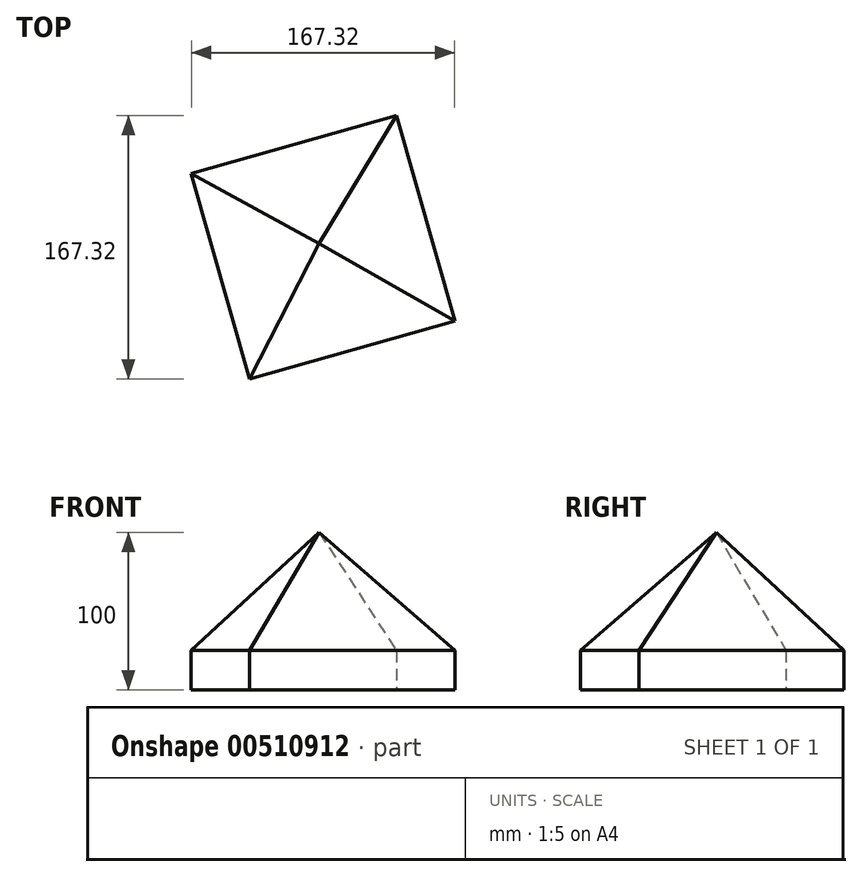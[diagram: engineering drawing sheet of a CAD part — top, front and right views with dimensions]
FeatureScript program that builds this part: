
annotation { "Feature Type Name" : "Feature", "Feature Type Description" : "" }
export const myFeature = defineFeature(function(context is Context, id is Id, definition is map)
    precondition{}
    {
        {
            var Q0;
            Q0=qCreatedBy(makeId("Top.planeOp"),FACE);
            var sketch = newSketch(context, id + "F0", { "sketchPlane" : qUnion([Q0])});
            skCircle(sketch, "E0.cCircle", {"center": v(0, 0) * mm, "radius": 95.85 * mm, "construction": true});
            skLineSegment(sketch, "E0.0", {"start": v(-46.76, -83.66) * mm, "end": v(-83.66, 46.76) * mm});
            skLineSegment(sketch, "E0.1", {"start": v(-83.66, 46.76) * mm, "end": v(46.76, 83.66) * mm});
            skLineSegment(sketch, "E0.2", {"start": v(46.76, 83.66) * mm, "end": v(83.66, -46.76) * mm});
            skLineSegment(sketch, "E0.3", {"start": v(83.66, -46.76) * mm, "end": v(-46.76, -83.66) * mm});
            skSolve(sketch);
        }
        {
            var Q0;
            Q0 = qSketchRegion(id + "F0", true);
            extrude(context, id + "F1", {"entities" : qUnion([Q0]), "depth" : 25 * mm});
        }
        {
            var Q0;
            Q0=qCreatedBy(makeId("Top.planeOp"),FACE);
            cPlane(context, id + "F2", {"entities" : qUnion([Q0]), "cplaneType" : CPlaneType.OFFSET, "offset" : 100 * mm, "width" : 150 * mm, "height" : 150 * mm});
        }
        {
            var Q0;
            Q0=qCreatedBy(id+"F2.planeOp",FACE);
            var sketch = newSketch(context, id + "F3", { "sketchPlane" : qUnion([Q0])});
            skPoint(sketch, "E1", {"position": v(-2.56, 2.4) * mm});
            skSolve(sketch);
        }
        {
            var Q1;
            Q1=sQuery(id+"F3.wireOp",VERTEX,"E1");
            var Q2;
            Q2=makeQuery(id+"F1.opExtrude","CAP_FACE",FACE,{"disambiguationData":[OSD([sQuery(id+"F0.wireOp",EDGE,"E0.0"),sQuery(id+"F0.wireOp",EDGE,"E0.1"),sQuery(id+"F0.wireOp",EDGE,"E0.2"),sQuery(id+"F0.wireOp",EDGE,"E0.3")])],"isStart":false});
            loft(context, id + "F4", {"operationType" : NewBodyOperationType.ADD, "sheetProfilesArray" : [{ "sheetProfileEntities" : qUnion([Q1]) }, { "sheetProfileEntities" : qUnion([Q2]) }]});
        }
    });
